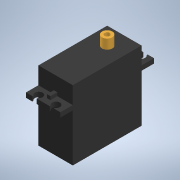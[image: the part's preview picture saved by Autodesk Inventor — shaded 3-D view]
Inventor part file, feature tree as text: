
AUTODESK INVENTOR PART (.ipt)
format: ipt  version: 2020 (Build 240168000, 168)  size: 216,064 bytes
history: native  units: in
note: dims shown in document units (in); Inventor stores cm internally (conversion verified against a paired STEP export)
features: extrude x7, sketch x7, projected_geometry x3, plane x1
ambient origin geometry x8: Origin, YZ Plane, XZ Plane, XY Plane, X Axis, Y Axis, Z Axis, Center Point
bodies: Solid1 (feature_tree)
feature tree (18):
  extrude  "Extrusion1"  Depth=1.5748in
  plane  "Work Plane1"
  extrude  "Extrusion2"  TaperAngle=0.0deg  [1 undecoded]
  extrude  "Extrusion3"  Depth=2.1457in
  extrude  "Extrusion4"  Depth=0.3937in
  extrude  "Extrusion5"  Depth=0.1063in TaperAngle=0.0deg
  extrude  "Extrusion6"  Depth=0.0787in
  extrude  "Extrusion7"  Depth=0.0787in TaperAngle=0.0deg
  sketch  "Sketch1"  dims[d0=0.7874in d1=1.5748in]
  sketch  "Sketch2"  dims[d2=1.0906in d3=0.0in d4=0.0in]
  projected_geometry  "Projected Loop1"
  sketch  "Sketch3"  dims[d5=0.5in d6=0.0in d7=2.1457in]
  projected_geometry  "Projected Loop2"
  sketch  "Sketch4"  dims[d8=0.3937in d9=1.9488in]
  sketch  "Sketch5"  dims[d10=0.1772in d11=0.1063in d12=0.0in]
  projected_geometry  "Projected Loop3"
  sketch  "Sketch6"  dims[d13=0.0984in d14=0.0787in]
  sketch  "Sketch7"  dims[d15=0.1575in d16=0.0787in d17=0.0in d18=0.2362in d19=1.1811in d20=0.2205in d21=0.0in d22=0.1181in d23=0.2205in d24=0.0in d25=0.252in d26=0.1575in d27=0.315in d28=0.2362in d29=0.0in]
note: 1 required parameter value undecoded (feature->parameter linkage not recoverable at this tier; creation-order binding heuristic only, values carry confidence <= 0.55)
